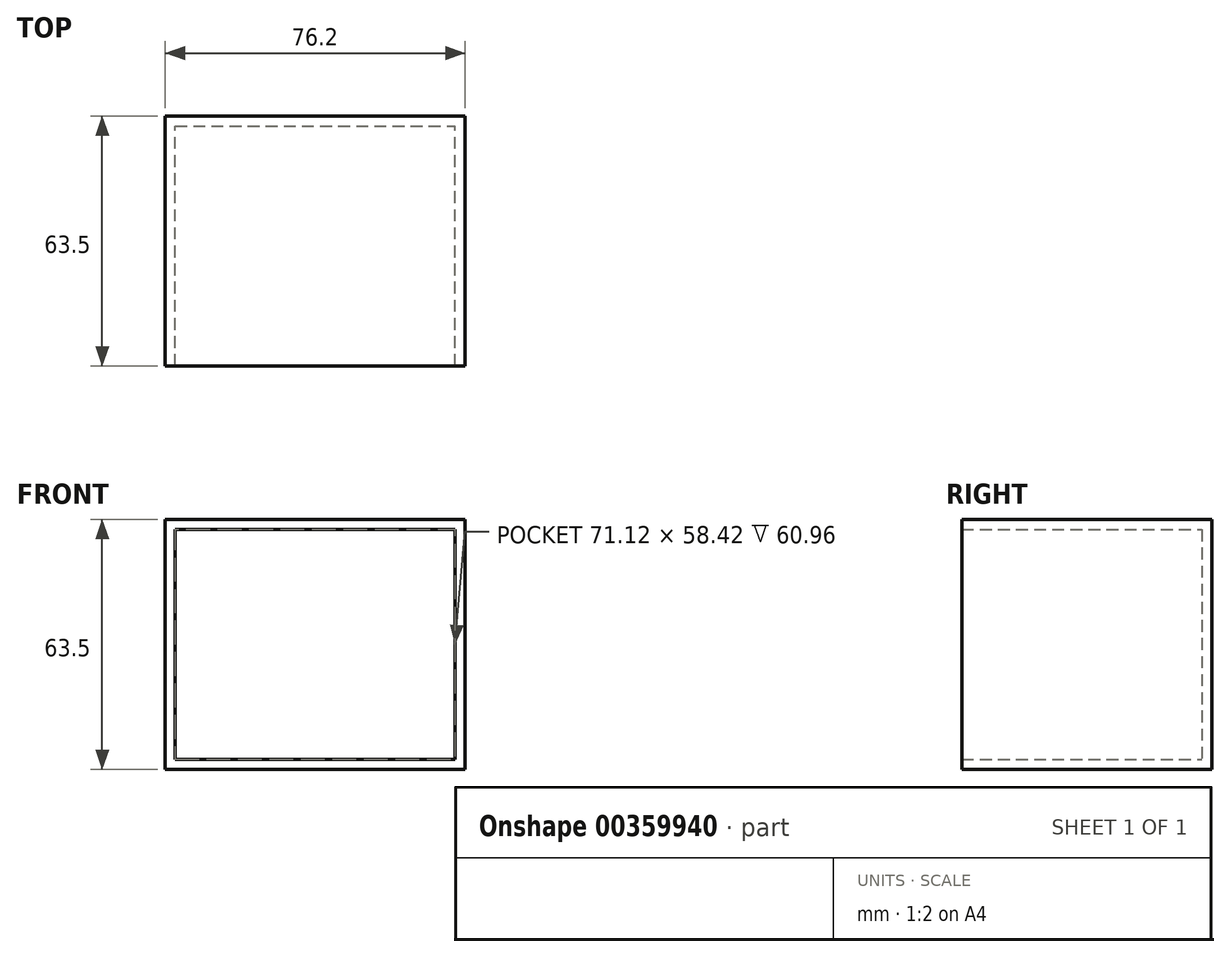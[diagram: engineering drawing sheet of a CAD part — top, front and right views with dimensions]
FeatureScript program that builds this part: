
annotation { "Feature Type Name" : "Feature", "Feature Type Description" : "" }
export const myFeature = defineFeature(function(context is Context, id is Id, definition is map)
    precondition{}
    {
        {
            var Q0;
            Q0=qCreatedBy(makeId("Front.planeOp"),FACE);
            var sketch = newSketch(context, id + "F0", { "sketchPlane" : qUnion([Q0])});
            skLineSegment(sketch, "E0.bottom", {"start": v(0, 0) * mm, "end": v(12.7, 0) * mm});
            skLineSegment(sketch, "E0.top", {"start": v(0, -63.5) * mm, "end": v(12.7, -63.5) * mm});
            skLineSegment(sketch, "E0.left", {"start": v(0, 0) * mm, "end": v(0, -63.5) * mm});
            skLineSegment(sketch, "E0.right", {"start": v(12.7, 0) * mm, "end": v(12.7, -63.5) * mm});
            skSolve(sketch);
        }
        {
            var Q0;
            Q0 = qSketchRegion(id + "F0", true);
            extrude(context, id + "F1", {"entities" : qUnion([Q0]), "depth" : 63.5 * mm});
        }
        {
            var Q0;
            Q0=makeQuery(id+"F1.opExtrude","SWEPT_FACE",FACE,{"disambiguationData":[OSD([sQuery(id+"F0.wireOp",EDGE,"E0.right")])]});
            extrude(context, id + "F2", {"entities" : qUnion([Q0]), "operationType" : NewBodyOperationType.ADD, "depth" : 63.5 * mm});
        }
        {
            var Q0;
            {var subQ0=sQuery(id+"F0.wireOp",EDGE,"E0.right");Q0=makeQuery(id+"F2.boolean.opBoolean","MERGE",FACE,{"derivedFrom":[makeQuery(id+"F1.opExtrude","CAP_FACE",FACE,{"disambiguationData":[OSD([sQuery(id+"F0.wireOp",EDGE,"E0.bottom"),sQuery(id+"F0.wireOp",EDGE,"E0.top"),sQuery(id+"F0.wireOp",EDGE,"E0.left"),subQ0])],"isStart":false}),makeQuery(id+"F2.opExtrude","SWEPT_FACE",FACE,{"disambiguationData":[OSD([subQ0]),TDD([makeQuery(id+"F1.opExtrude","CAP_EDGE",EDGE,{"disambiguationData":[OSD([subQ0])],"isStart":false})])]})]});}
            shell(context, id + "F3", {"entities" : qUnion([Q0]), "thickness" : 2.54 * mm});
        }
    });
